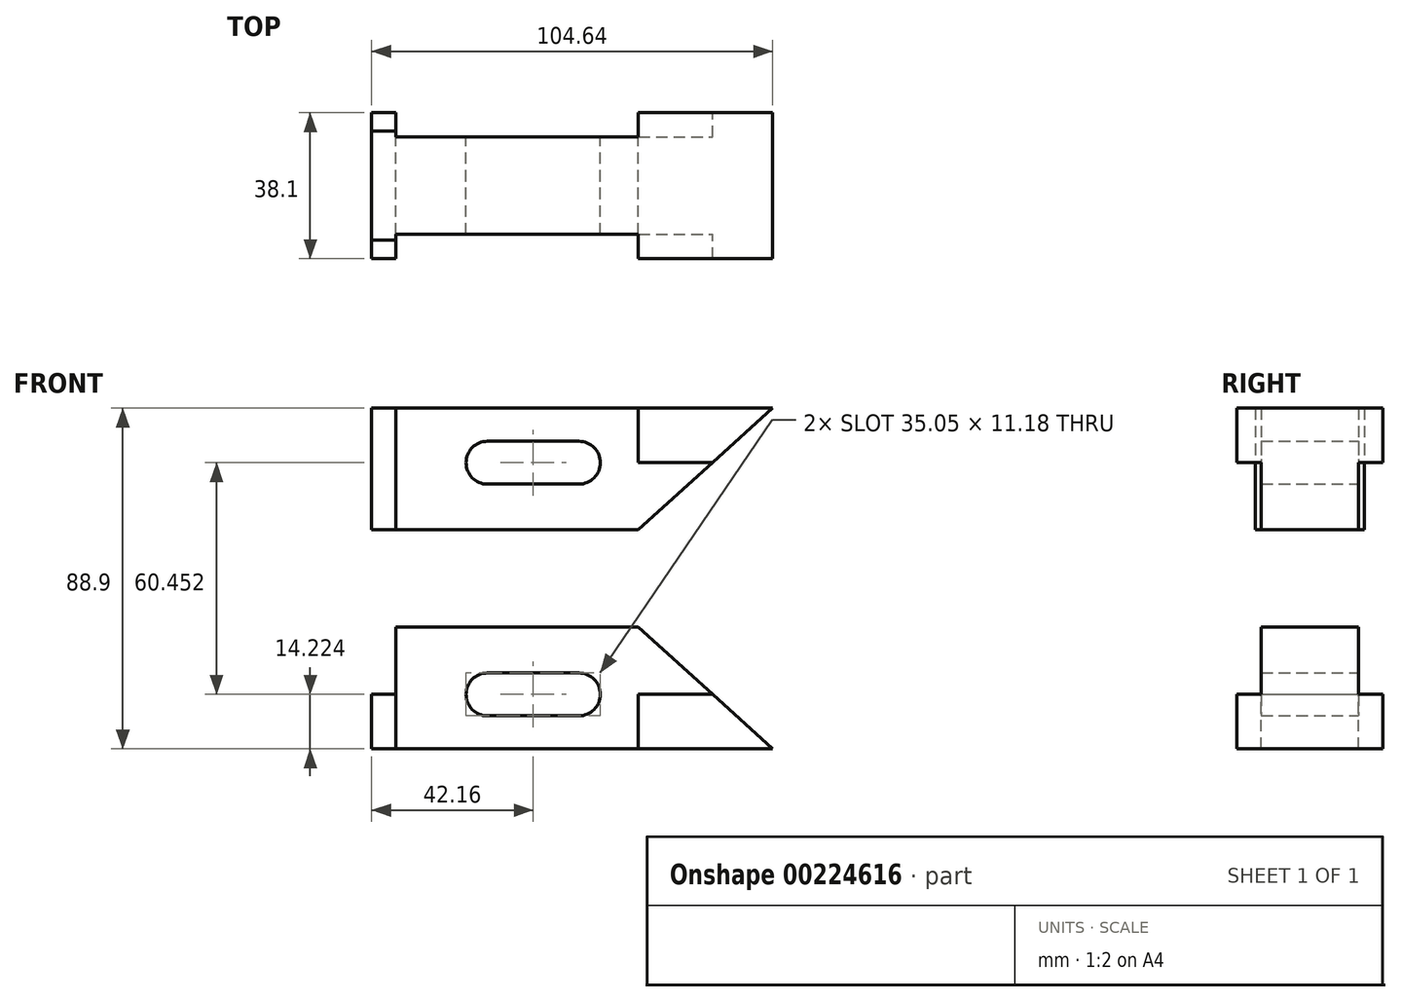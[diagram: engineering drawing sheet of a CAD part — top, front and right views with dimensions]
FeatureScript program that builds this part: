
annotation { "Feature Type Name" : "Feature", "Feature Type Description" : "" }
export const myFeature = defineFeature(function(context is Context, id is Id, definition is map)
    precondition{}
    {
        {
            var Q0;
            Q0=qCreatedBy(makeId("Front.planeOp"),FACE);
            var sketch = newSketch(context, id + "F0", { "sketchPlane" : qUnion([Q0])});
            skLineSegment(sketch, "E0.bottom", {"start": v(-52.32, 44.45) * mm, "end": v(52.32, 44.45) * mm});
            skLineSegment(sketch, "E0.top", {"start": v(-52.32, -44.45) * mm, "end": v(52.32, -44.45) * mm});
            skLineSegment(sketch, "E0.left", {"start": v(-52.32, 44.45) * mm, "end": v(-52.32, -44.45) * mm});
            skLineSegment(sketch, "E0.right", {"start": v(52.32, 44.45) * mm, "end": v(52.32, -44.45) * mm});
            skPoint(sketch, "E0.middle", {"position": v(0, 0) * mm});
            skLineSegment(sketch, "E1", {"start": v(-52.32, -44.45) * mm, "end": v(-52.32, -30.23) * mm});
            skLineSegment(sketch, "E2", {"start": v(-52.32, -30.23) * mm, "end": v(-22.1, -30.23) * mm});
            skLineSegment(sketch, "E3", {"start": v(-22.1, -30.23) * mm, "end": v(1.78, -30.23) * mm});
            skLineSegment(sketch, "E4.MirrorCS", {"start": v(-22.1, 30.23) * mm, "end": v(1.78, 30.23) * mm});
            skCircle(sketch, "E5", {"center": v(-22.1, 30.23) * mm, "radius": 5.59 * mm});
            skCircle(sketch, "E6", {"center": v(1.78, 30.23) * mm, "radius": 5.59 * mm});
            skCircle(sketch, "E7.MirrorC", {"center": v(-22.1, -30.23) * mm, "radius": 5.59 * mm});
            skCircle(sketch, "E8.MirrorC", {"center": v(1.78, -30.23) * mm, "radius": 5.59 * mm});
            skLineSegment(sketch, "E9", {"start": v(-22.1, -30.23) * mm, "end": v(-22.1, -24.64) * mm});
            skLineSegment(sketch, "E10", {"start": v(-22.1, -30.23) * mm, "end": v(-22.1, -35.81) * mm});
            skLineSegment(sketch, "E11", {"start": v(1.78, -30.23) * mm, "end": v(1.78, -24.64) * mm});
            skLineSegment(sketch, "E12", {"start": v(1.78, -24.64) * mm, "end": v(1.78, -35.81) * mm});
            skLineSegment(sketch, "E13", {"start": v(-22.1, -24.64) * mm, "end": v(1.78, -24.64) * mm});
            skLineSegment(sketch, "E14", {"start": v(-22.1, -35.81) * mm, "end": v(1.78, -35.81) * mm});
            skLineSegment(sketch, "E15.MirrorCS", {"start": v(-22.1, 35.81) * mm, "end": v(1.78, 35.81) * mm});
            skLineSegment(sketch, "E16.MirrorCS", {"start": v(-22.1, 24.64) * mm, "end": v(1.78, 24.64) * mm});
            skLineSegment(sketch, "E17", {"start": v(-52.32, -44.45) * mm, "end": v(-45.97, -44.45) * mm});
            skLineSegment(sketch, "E18", {"start": v(-45.97, -44.45) * mm, "end": v(-45.97, -12.7) * mm});
            skLineSegment(sketch, "E19", {"start": v(-52.32, -30.23) * mm, "end": v(-52.32, -12.7) * mm});
            skLineSegment(sketch, "E20", {"start": v(-52.32, -12.7) * mm, "end": v(-45.97, -12.7) * mm});
            skLineSegment(sketch, "E21.MirrorCS", {"start": v(-52.32, 12.7) * mm, "end": v(-45.97, 12.7) * mm});
            skLineSegment(sketch, "E22.MirrorCS", {"start": v(-52.32, 44.45) * mm, "end": v(-45.97, 44.45) * mm});
            skLineSegment(sketch, "E23.MirrorCS", {"start": v(-52.32, 44.45) * mm, "end": v(-52.32, 30.23) * mm});
            skLineSegment(sketch, "E24.MirrorCS", {"start": v(-52.32, 30.23) * mm, "end": v(-52.32, 12.7) * mm});
            skLineSegment(sketch, "E25.MirrorCS", {"start": v(-45.97, 44.45) * mm, "end": v(-45.97, 12.7) * mm});
            skLineSegment(sketch, "E26", {"start": v(-52.32, -44.45) * mm, "end": v(17.27, -44.45) * mm});
            skLineSegment(sketch, "E27", {"start": v(-52.32, 44.45) * mm, "end": v(17.27, 44.45) * mm});
            skLineSegment(sketch, "E28", {"start": v(17.27, -44.45) * mm, "end": v(17.27, -30.23) * mm});
            skLineSegment(sketch, "E29.MirrorCS", {"start": v(17.27, 44.45) * mm, "end": v(17.27, 30.23) * mm});
            skLineSegment(sketch, "E30", {"start": v(-45.97, -12.7) * mm, "end": v(17.27, -12.7) * mm});
            skLineSegment(sketch, "E31.MirrorCS", {"start": v(-45.97, 12.7) * mm, "end": v(17.27, 12.7) * mm});
            skLineSegment(sketch, "E32", {"start": v(17.27, -12.7) * mm, "end": v(52.32, -44.45) * mm});
            skLineSegment(sketch, "E33", {"start": v(17.27, 12.7) * mm, "end": v(52.32, 44.45) * mm});
            skLineSegment(sketch, "E34", {"start": v(17.27, 30.23) * mm, "end": v(36.62, 30.23) * mm});
            skLineSegment(sketch, "E35", {"start": v(17.27, -30.23) * mm, "end": v(36.62, -30.23) * mm});
            skLineSegment(sketch, "E36", {"start": v(17.27, 12.7) * mm, "end": v(17.27, -12.7) * mm});
            skSolve(sketch);
        }
        {
            var Q0;
            Q0=makeQuery(id+"F0.imprint","IMPRINT",FACE,{"disambiguationData":[TD([[makeQuery(id+"F0.imprint","IMPRINT",EDGE,{"derivedFrom":sQuery(id+"F0.wireOp",EDGE,"E0.left")}),1.0]])]});
            extrude(context, id + "F1", {"entities" : qUnion([Q0]), "endBound" : BoundingType.SYMMETRIC, "depth" : 28.45 * mm});
        }
        {
            var Q0;
            Q0=makeQuery(id+"F0.imprint","IMPRINT",FACE,{"disambiguationData":[TD([[makeQuery(id+"F0.imprint","IMPRINT",EDGE,{"derivedFrom":sQuery(id+"F0.wireOp",EDGE,"E21.MirrorCS")}),1.0]])]});
            var Q1;
            {var subQ0=sQuery(id+"F0.wireOp",EDGE,"E19");Q1=makeQuery(id+"F0.imprint","IMPRINT",FACE,{"disambiguationData":[TD([[makeQuery(id+"F0.imprint","IMPRINT",EDGE,{"derivedFrom":subQ0}),-1.0]])]});}
            var Q2;
            {var subQ0=sQuery(id+"F0.wireOp",EDGE,"E1");Q2=makeQuery(id+"F0.imprint","IMPRINT",FACE,{"disambiguationData":[TD([[makeQuery(id+"F0.imprint","IMPRINT",EDGE,{"derivedFrom":subQ0}),-1.0]])]});}
            extrude(context, id + "F2", {"entities" : qUnion([Q0, Q1, Q2]), "operationType" : NewBodyOperationType.ADD, "oppositeDirection" : true, "depth" : 4.83 * mm});
        }
        {
            var Q0;
            {var subQ1=sQuery(id+"F0.wireOp",EDGE,"E15.MirrorCS");Q0=makeQuery(id+"F0.imprint","IMPRINT",FACE,{"disambiguationData":[TD([[makeQuery(id+"F0.imprint","IMPRINT",EDGE,{"derivedFrom":subQ1}),1.0]])]});}
            extrude(context, id + "F3", {"entities" : qUnion([Q0]), "operationType" : NewBodyOperationType.ADD, "endBound" : BoundingType.SYMMETRIC, "depth" : 25.4 * mm});
        }
        {
            var Q0;
            {var subQ12=sQuery(id+"F0.wireOp",EDGE,"E13");Q0=makeQuery(id+"F0.imprint","IMPRINT",FACE,{"disambiguationData":[TD([[makeQuery(id+"F0.imprint","IMPRINT",EDGE,{"derivedFrom":subQ12}),1.0]])]});}
            extrude(context, id + "F4", {"entities" : qUnion([Q0]), "operationType" : NewBodyOperationType.ADD, "endBound" : BoundingType.SYMMETRIC, "depth" : 25.4 * mm});
        }
        {
            var Q0;
            {var subQ0=sQuery(id+"F0.wireOp",EDGE,"E0.bottom");Q0=makeQuery(id+"F0.imprint","IMPRINT",FACE,{"disambiguationData":[TD([[makeQuery(id+"F0.imprint","IMPRINT",EDGE,{"derivedFrom":subQ0}),-1.0]])]});}
            var Q1;
            {var subQ0=sQuery(id+"F0.wireOp",EDGE,"E0.top");Q1=makeQuery(id+"F0.imprint","IMPRINT",FACE,{"disambiguationData":[TD([[makeQuery(id+"F0.imprint","IMPRINT",EDGE,{"derivedFrom":subQ0}),1.0]])]});}
            extrude(context, id + "F5", {"entities" : qUnion([Q0, Q1]), "operationType" : NewBodyOperationType.ADD, "endBound" : BoundingType.SYMMETRIC, "depth" : 38.1 * mm});
        }
    });
